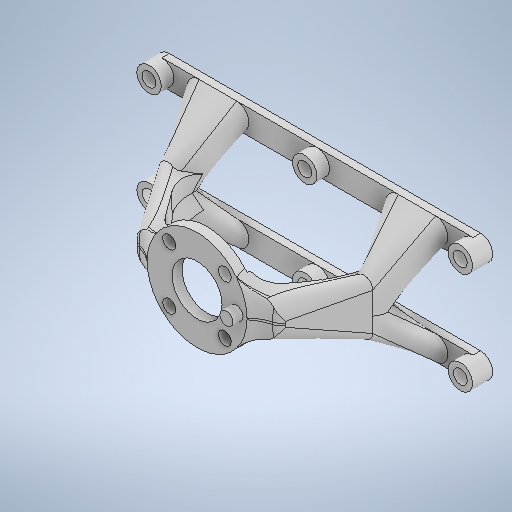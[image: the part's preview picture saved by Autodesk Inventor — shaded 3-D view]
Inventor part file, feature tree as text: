
AUTODESK INVENTOR PART (.ipt)
format: ipt  version: 2025.1 (Build 291241000, 241)  size: 1,214,464 bytes
history: native  units: mm
features: sketch x7, loft x6, extrude x5, fillet x5, plane x2
ambient origin geometry x8: Origin, YZ Plane, XZ Plane, XY Plane, X Axis, Y Axis, Z Axis, Center Point
bodies: Solid1 (feature_tree)
feature tree (25):
  sketch  "Sketch1"  dims[d0=20.0mm d1=40.0mm]
  extrude  "Extrusion1"  Depth=40.0mm
  extrude  "Extrusion2"  Depth=5.2mm
  plane  "Work Plane1"
  sketch  "Sketch2"  dims[d9=5.3mm d10=4.0mm d11=0.0mm]
  plane  "Work Plane2"
  sketch  "Sketch3"  dims[d12=8.0mm d13=0.0mm d14=47.2mm]
  extrude  "Extrusion3"  Depth=40.0mm TaperAngle=360.0deg
  sketch  "Sketch4"  dims[d15=9.8mm d17=5.6mm]
  loft  "Loft1"
  loft  "Loft2"
  loft  "Loft3"
  loft  "Loft4"
  loft  "Loft5"
  loft  "Loft6"
  fillet  "Fillet1"  Radius=15.0mm
  fillet  "Fillet2"  Radius=3.0mm
  fillet  "Fillet3"  Radius=15.0mm
  fillet  "Fillet4"  Radius=15.0mm
  fillet  "Fillet5"  [1 undecoded]
  extrude  "Extrusion4"  TaperAngle=0.0deg  [1 undecoded]
  extrude  "Extrusion5"  TaperAngle=0.0deg  [1 undecoded]
  sketch  "Sketch Circular Pattern1"  dims[d2=31.5mm d3=5.2mm]
  sketch  "Sketch Rectangular Pattern1"  dims[d4=45.0deg d5=40.0mm d7=360.0deg]
  sketch  "Sketch5"  dims[d18=134.5mm d19=30.0mm d21=62.35mm d22=10.0mm d24=10.0mm d26=40.8mm d27=7.0mm d28=15.0mm d29=3.0mm d30=0.0mm d31=15.0mm d32=15.0mm d33=0.0mm d34=90.0deg d35=0.0mm d36=90.0deg d37=0.0mm d38=90.0deg d39=0.0mm d40=90.0deg d41=0.0mm d42=90.0deg d43=0.0mm d44=90.0deg d45=0.0mm d46=90.0deg d47=0.0mm d48=90.0deg d49=10.0mm d50=15.0mm d51=7.0mm d52=0.0mm d53=90.0deg d54=0.0mm d55=90.0deg d56=15.0mm d57=10.0mm d58=7.0mm d59=0.0mm d60=90.0deg d61=0.0mm d62=90.0deg d63=17.0mm d64=17.0mm d65=17.0mm d66=17.0mm d67=5.0mm d68=8.1mm d69=0.0mm d70=10.0mm d71=10.0mm d72=10.0mm d73=10.0mm d74=2.0mm d75=0.0mm]
note: 3 required parameter values undecoded (feature->parameter linkage not recoverable at this tier; creation-order binding heuristic only, values carry confidence <= 0.55)
